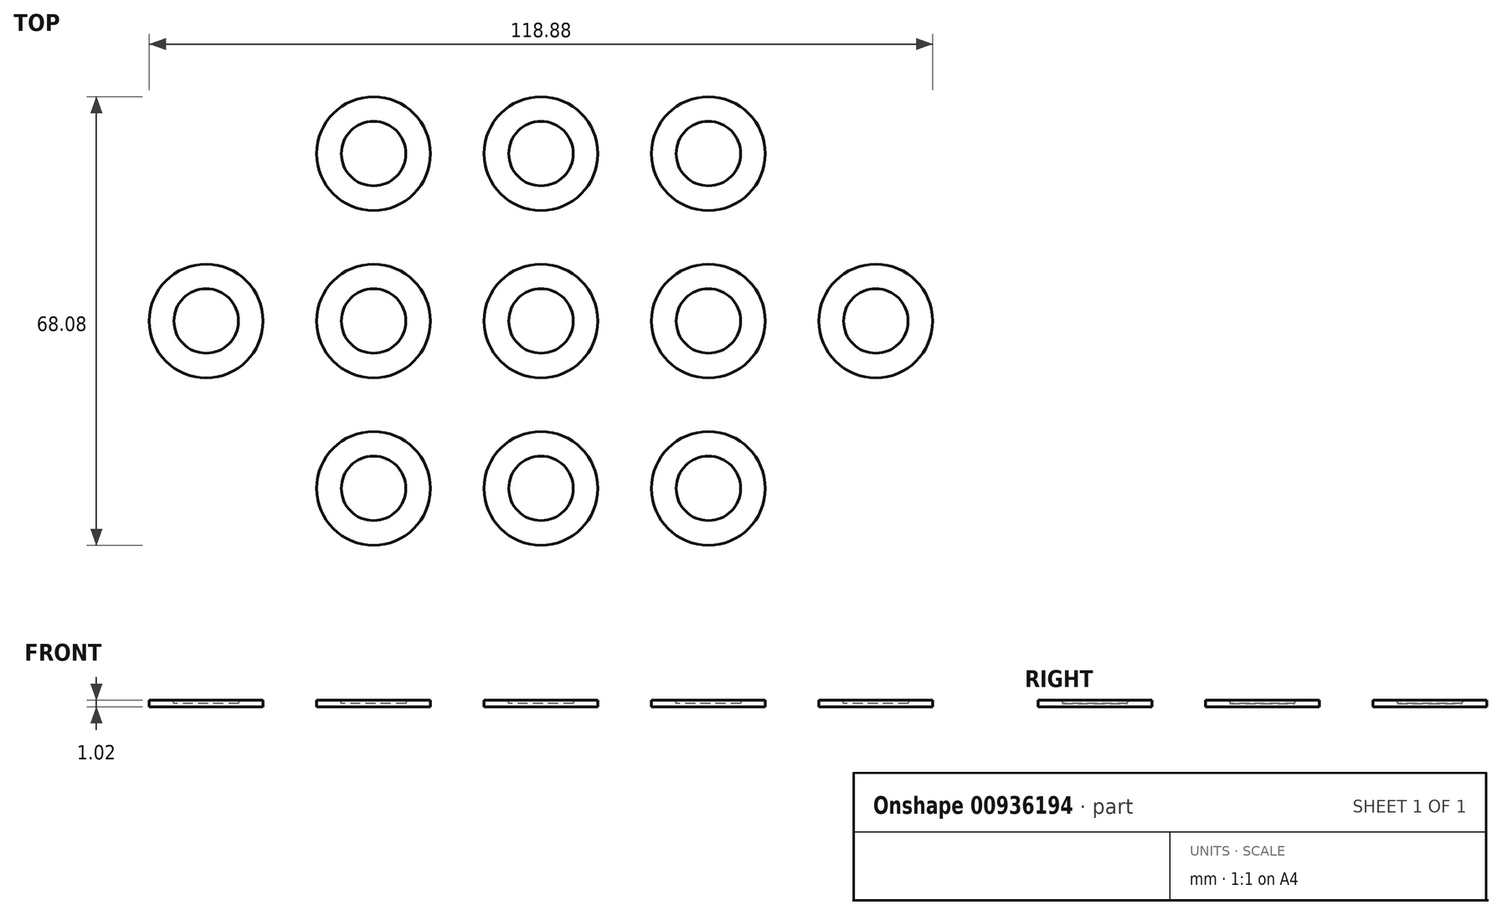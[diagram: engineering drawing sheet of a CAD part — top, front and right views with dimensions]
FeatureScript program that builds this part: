
annotation { "Feature Type Name" : "Feature", "Feature Type Description" : "" }
export const myFeature = defineFeature(function(context is Context, id is Id, definition is map)
    precondition{}
    {
        {
            var Q0;
            Q0=qCreatedBy(makeId("Top.planeOp"),FACE);
            var sketch = newSketch(context, id + "F0", { "sketchPlane" : qUnion([Q0])});
            skCircle(sketch, "E0", {"center": v(0, 0) * mm, "radius": 8.64 * mm});
            skCircle(sketch, "E1", {"center": v(0, 0) * mm, "radius": 4.89 * mm});
            skSolve(sketch);
        }
        {
            var Q0;
            Q0=makeQuery(id+"F0.imprint","IMPRINT",FACE,{"disambiguationData":[TD([[makeQuery(id+"F0.imprint","IMPRINT",EDGE,{"derivedFrom":sQuery(id+"F0.wireOp",EDGE,"E1")}),1.0]])]});
            extrude(context, id + "F1", {"entities" : qUnion([Q0]), "depth" : 0.5 * mm, "offsetDistance" : 25.4 * mm});
        }
        {
            var Q0;
            Q0=makeQuery(id+"F0.imprint","IMPRINT",FACE,{"disambiguationData":[TD([[makeQuery(id+"F0.imprint","IMPRINT",EDGE,{"derivedFrom":sQuery(id+"F0.wireOp",EDGE,"E0")}),1.0]])]});
            extrude(context, id + "F2", {"entities" : qUnion([Q0]), "operationType" : NewBodyOperationType.ADD, "depth" : 1.02 * mm, "offsetDistance" : 25.4 * mm});
        }
        {
            var Q0;
            Q0=makeQuery(id+"F2.opExtrude","CAP_EDGE",EDGE,{"disambiguationData":[OSD([sQuery(id+"F0.wireOp",EDGE,"E1")])],"isStart":false});
            fillet(context, id + "F3", {"entities" : qUnion([Q0]), "radius" : 0.5 * mm, "tangentPropagation" : true, "allowEdgeOverflow" : false});
        }
        {
            var Q0;
            Q0=makeQuery(id+"F1.opExtrude","SWEPT_BODY",BODY,{"disambiguationData":[OSD([sQuery(id+"F0.wireOp",EDGE,"E1")])]});
            transform(context, id + "F4", {"entities" : qUnion([Q0]), "transformType" : TransformType.TRANSLATION_3D, "dx" : 0 * mm, "dy" : 25.4 * mm, "dz" : 0 * mm, "makeCopy" : true});
        }
        {
            var Q0;
            Q0=makeQuery(id+"F1.opExtrude","SWEPT_BODY",BODY,{"disambiguationData":[OSD([sQuery(id+"F0.wireOp",EDGE,"E1")])]});
            transform(context, id + "F5", {"entities" : qUnion([Q0]), "transformType" : TransformType.TRANSLATION_3D, "dx" : 0 * mm, "dy" : -25.4 * mm, "dz" : 0 * mm, "makeCopy" : true});
        }
        {
            var Q0;
            Q0=makeQuery(id+"F1.opExtrude","SWEPT_BODY",BODY,{"disambiguationData":[OSD([sQuery(id+"F0.wireOp",EDGE,"E1")])]});
            transform(context, id + "F6", {"entities" : qUnion([Q0]), "transformType" : TransformType.TRANSLATION_3D, "dx" : 25.4 * mm, "dy" : 0 * mm, "dz" : 0 * mm, "makeCopy" : true});
        }
        {
            var Q0;
            Q0=makeQuery(id+"F1.opExtrude","SWEPT_BODY",BODY,{"disambiguationData":[OSD([sQuery(id+"F0.wireOp",EDGE,"E1")])]});
            transform(context, id + "F7", {"entities" : qUnion([Q0]), "transformType" : TransformType.TRANSLATION_3D, "dx" : -25.4 * mm, "dy" : 0 * mm, "dz" : 0 * mm, "makeCopy" : true});
        }
        {
            var Q0;
            Q0=makeQuery(id+"F6.opPattern","COPY",BODY,{"derivedFrom":makeQuery(id+"F1.opExtrude","SWEPT_BODY",BODY,{"disambiguationData":[OSD([sQuery(id+"F0.wireOp",EDGE,"E1")])]}),"instanceName":"1"});
            transform(context, id + "F8", {"entities" : qUnion([Q0]), "transformType" : TransformType.TRANSLATION_3D, "dx" : 25.4 * mm, "dy" : 0 * mm, "dz" : 0 * mm, "makeCopy" : true});
        }
        {
            var Q0;
            Q0=makeQuery(id+"F7.opPattern","COPY",BODY,{"derivedFrom":makeQuery(id+"F1.opExtrude","SWEPT_BODY",BODY,{"disambiguationData":[OSD([sQuery(id+"F0.wireOp",EDGE,"E1")])]}),"instanceName":"1"});
            transform(context, id + "F9", {"entities" : qUnion([Q0]), "transformType" : TransformType.TRANSLATION_3D, "dx" : -25.4 * mm, "dy" : 0 * mm, "dz" : 0 * mm, "makeCopy" : true});
        }
        {
            var Q0;
            Q0=makeQuery(id+"F7.opPattern","COPY",BODY,{"derivedFrom":makeQuery(id+"F1.opExtrude","SWEPT_BODY",BODY,{"disambiguationData":[OSD([sQuery(id+"F0.wireOp",EDGE,"E1")])]}),"instanceName":"1"});
            transform(context, id + "F10", {"entities" : qUnion([Q0]), "transformType" : TransformType.TRANSLATION_3D, "dx" : 0 * mm, "dy" : -25.4 * mm, "dz" : 0 * mm, "makeCopy" : true});
        }
        {
            var Q0;
            Q0=makeQuery(id+"F7.opPattern","COPY",BODY,{"derivedFrom":makeQuery(id+"F1.opExtrude","SWEPT_BODY",BODY,{"disambiguationData":[OSD([sQuery(id+"F0.wireOp",EDGE,"E1")])]}),"instanceName":"1"});
            transform(context, id + "F11", {"entities" : qUnion([Q0]), "transformType" : TransformType.TRANSLATION_3D, "dx" : 0 * mm, "dy" : 25.4 * mm, "dz" : 0 * mm, "makeCopy" : true});
        }
        {
            var Q0;
            Q0=makeQuery(id+"F6.opPattern","COPY",BODY,{"derivedFrom":makeQuery(id+"F1.opExtrude","SWEPT_BODY",BODY,{"disambiguationData":[OSD([sQuery(id+"F0.wireOp",EDGE,"E1")])]}),"instanceName":"1"});
            transform(context, id + "F12", {"entities" : qUnion([Q0]), "transformType" : TransformType.TRANSLATION_3D, "dx" : 0 * mm, "dy" : -25.4 * mm, "dz" : 0 * mm, "makeCopy" : true});
        }
        {
            var Q0;
            Q0=makeQuery(id+"F6.opPattern","COPY",BODY,{"derivedFrom":makeQuery(id+"F1.opExtrude","SWEPT_BODY",BODY,{"disambiguationData":[OSD([sQuery(id+"F0.wireOp",EDGE,"E1")])]}),"instanceName":"1"});
            transform(context, id + "F13", {"entities" : qUnion([Q0]), "transformType" : TransformType.TRANSLATION_3D, "dx" : 0 * mm, "dy" : 25.4 * mm, "dz" : 0 * mm, "makeCopy" : true});
        }
    });
